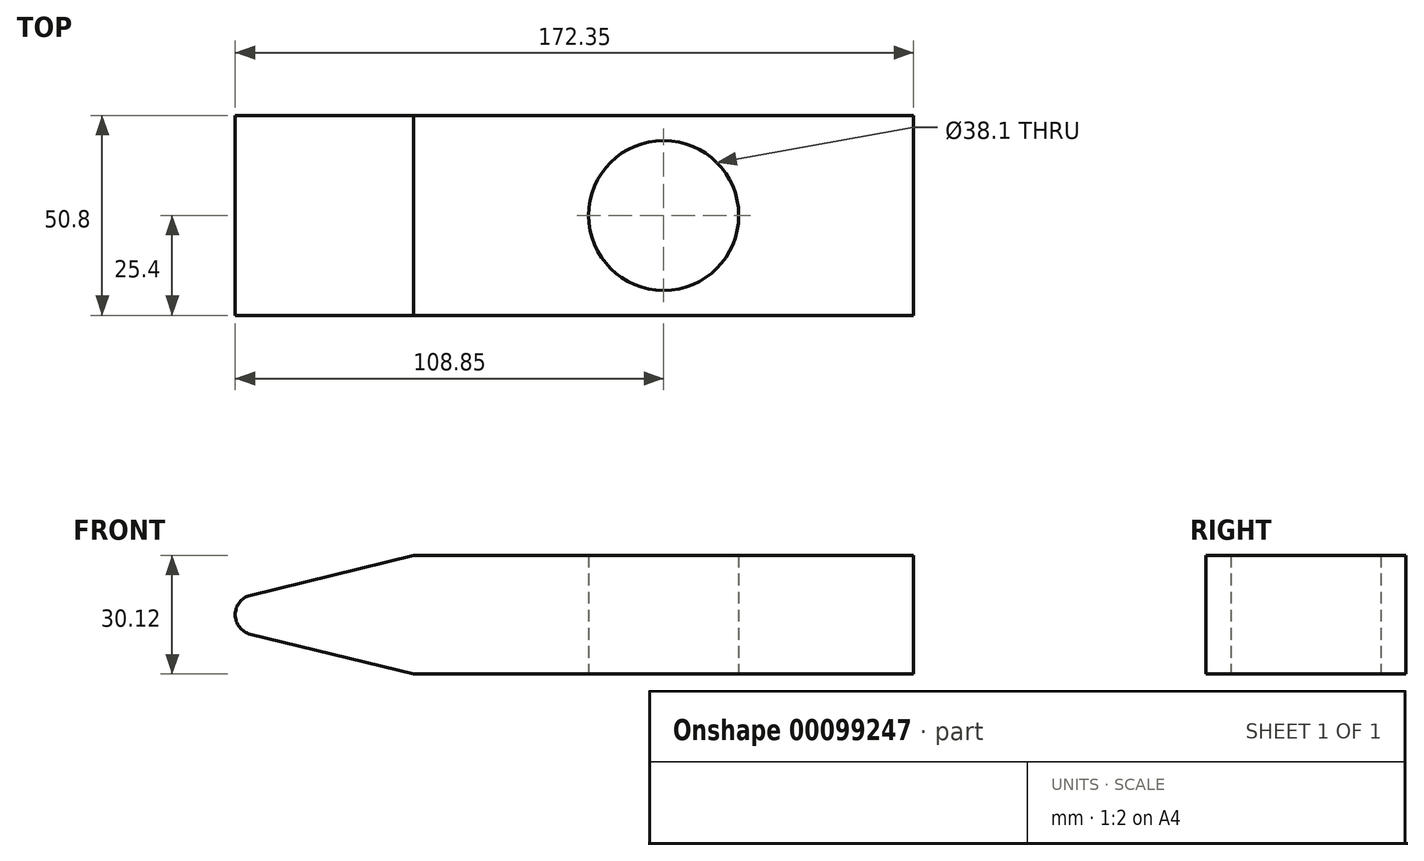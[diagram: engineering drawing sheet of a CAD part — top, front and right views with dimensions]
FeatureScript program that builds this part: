
annotation { "Feature Type Name" : "Feature", "Feature Type Description" : "" }
export const myFeature = defineFeature(function(context is Context, id is Id, definition is map)
    precondition{}
    {
        {
            var Q0;
            Q0=qCreatedBy(makeId("Front.planeOp"),FACE);
            var sketch = newSketch(context, id + "F0", { "sketchPlane" : qUnion([Q0])});
            skLineSegment(sketch, "E0.bottom", {"start": v(-63.5, 15.06) * mm, "end": v(63.5, 15.06) * mm});
            skLineSegment(sketch, "E0.top", {"start": v(-63.5, -15.06) * mm, "end": v(63.5, -15.06) * mm});
            skLineSegment(sketch, "E0.left", {"start": v(-63.5, 15.06) * mm, "end": v(-63.5, -15.06) * mm});
            skLineSegment(sketch, "E0.right", {"start": v(63.5, 15.06) * mm, "end": v(63.5, -15.06) * mm});
            skPoint(sketch, "E0.middle", {"position": v(0, 0) * mm});
            skLineSegment(sketch, "E1", {"start": v(-63.5, -15.06) * mm, "end": v(-125.19, 0) * mm});
            skLineSegment(sketch, "E2", {"start": v(-125.19, 0) * mm, "end": v(-63.5, 15.06) * mm});
            skSolve(sketch);
        }
        {
            var Q0;
            Q0=makeQuery(id+"F0.imprint","IMPRINT",FACE,{"disambiguationData":[TD([[makeQuery(id+"F0.imprint","IMPRINT",EDGE,{"derivedFrom":sQuery(id+"F0.wireOp",EDGE,"E0.bottom")}),-1.0]])]});
            var Q1;
            Q1=makeQuery(id+"F0.imprint","IMPRINT",FACE,{"disambiguationData":[TD([[makeQuery(id+"F0.imprint","IMPRINT",EDGE,{"derivedFrom":sQuery(id+"F0.wireOp",EDGE,"E0.left")}),-1.0]])]});
            extrude(context, id + "F1", {"entities" : qUnion([Q0, Q1]), "depth" : 25.4 * mm, "hasSecondDirection" : true, "secondDirectionOppositeDirection" : true, "secondDirectionDepth" : 25.4 * mm});
        }
        {
            var Q0;
            Q0=qCreatedBy(makeId("Top.planeOp"),FACE);
            var sketch = newSketch(context, id + "F2", { "sketchPlane" : qUnion([Q0])});
            skCircle(sketch, "E3", {"center": v(0, 0) * mm, "radius": 19.05 * mm});
            skSolve(sketch);
        }
        {
            var Q0;
            Q0 = qSketchRegion(id + "F2", true);
            extrude(context, id + "F3", {"entities" : qUnion([Q0]), "operationType" : NewBodyOperationType.REMOVE, "endBound" : BoundingType.THROUGH_ALL, "depth" : 254 * mm, "hasSecondDirection" : true, "secondDirectionBound" : SecondDirectionBoundingType.UP_TO_NEXT, "secondDirectionOppositeDirection" : true, "secondDirectionDepth" : 254 * mm});
        }
        {
            var Q0;
            Q0=makeQuery(id+"F1.opExtrude","SWEPT_EDGE",EDGE,{"disambiguationData":[OSD([sQuery(id+"F0.wireOp",EDGE,"E1"),sQuery(id+"F0.wireOp",EDGE,"E2")])]});
            fillet(context, id + "F4", {"entities" : qUnion([Q0]), "radius" : 5.08 * mm, "tangentPropagation" : true, "allowEdgeOverflow" : false});
        }
    });
